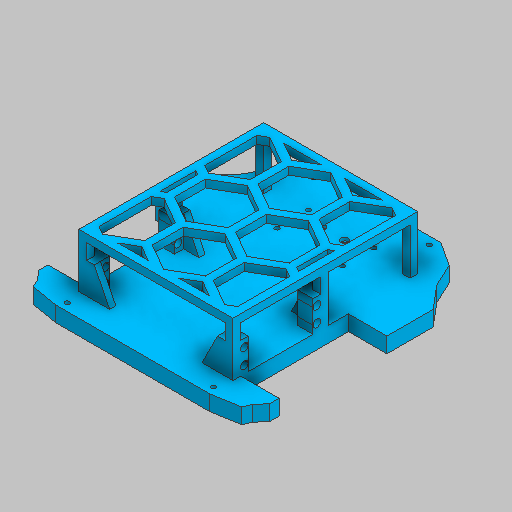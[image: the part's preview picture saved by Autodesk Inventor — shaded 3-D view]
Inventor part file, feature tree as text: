
AUTODESK INVENTOR PART (.ipt)
format: ipt  version: 2025 (Build 290162010, 162A)  size: 1,139,712 bytes
history: native  units: mm
features: other x22, extrude x15, sketch x15
ambient origin geometry x8: Origin, YZ Plane, XZ Plane, XY Plane, X Axis, Y Axis, Z Axis, Center Point
bodies: Body1 (feature_tree)
feature tree (52):
  other  "Sólido1"
  extrude  "Base"  Depth=10.0mm TaperAngle=0.0deg
  extrude  "Llantas"  Depth=70.0mm
  extrude  "Carroceria"  Depth=75.0mm
  extrude  "Tornillos Chasis 1"  Depth=150.0mm
  extrude  "Tornillos Chasis 2"  Depth=10.0mm TaperAngle=0.0deg
  extrude  "Soporte Rueda 1"  Depth=30.0mm
  extrude  "Soporte Rueda 2"  Depth=40.0mm
  extrude  "Soporte Motor 1"  Depth=15.0mm
  extrude  "Soporte Motor 2"  Depth=6.0mm
  extrude  "Soporte Motor 3"  Depth=11.34464mm
  extrude  "Soporte Motor 4"  Depth=5.0mm
  extrude  "Soporte ESP 1"  Depth=5.0mm
  extrude  "Soporte ESP 2"  Depth=37.5mm
  extrude  "Extrusión38"  Depth=5.0mm
  extrude  "Extrusión39"  Depth=10.0mm TaperAngle=0.0deg
  sketch  "Boceto Base"  dims[d44=37.5mm d45=3.0mm]
  sketch  "Boceto Llantas"  dims[d46=5.0mm d47=3.0mm]
  sketch  "Boceto Carroceria"  dims[d48=47.5mm d49=10.0mm d50=0.0mm d81=5.0mm d82=5.0mm d83=5.0mm d84=5.0mm d85=2.0mm d86=0.0mm d244=10.0mm d245=10.0mm d247=10.0mm d248=10.0mm d249=5.0mm d250=42.0mm d251=20.0mm d252=0.0mm d253=5.0mm d254=5.0mm d255=5.0mm d256=5.0mm d257=5.0mm d258=5.0mm d259=10.0mm d260=10.0mm d261=100.0mm d262=0.0mm d263=4.0mm d264=4.0mm d265=10.0mm d266=10.0mm d267=20.0mm d268=0.0mm d269=10.0mm d270=10.0mm d271=100.0mm d272=0.0mm d273=3.0mm d274=35.0mm d275=21.3mm d276=21.3mm d277=3.0mm d278=20.3mm d279=20.0mm d280=0.0mm d281=5.0mm d282=5.0mm d283=5.0mm d284=5.0mm d285=2.0mm d286=0.0mm d287=3.0mm d288=3.0mm d289=50.0mm d290=50.0mm d291=7.5mm d292=7.5mm d293=20.0mm d294=0.0mm d299=5.0mm d300=5.0mm d301=2.0mm d302=0.0mm d303=115.0mm d304=0.0mm d305=5.0mm d306=5.0mm d307=30.0mm d308=0.0mm d329=20.0mm d330=20.0mm d331=120.0deg d332=20.0mm d333=120.0deg d334=20.0mm d335=120.0deg d336=20.0mm d337=120.0deg d338=20.0mm d339=120.0deg d340=0.0mm d341=0.0mm d354=5.0mm d355=0.0mm d64=0.5mm d65=0.872665mm d66=0.5mm d67=0.872665mm d229=0.5mm d230=0.872665mm d231=0.5mm d232=0.872665mm]
  sketch  "Boceto Tornillos Chasis 1"  dims[d0=160.0mm d2=10.0mm d3=0.0mm]
  sketch  "Boceto Tornillos Chasis 2"  dims[d4=70.0mm d5=70.0mm]
  sketch  "Boceto27"  dims[d6=20.0mm d7=75.0mm]
  sketch  "Boceto28"  dims[d8=80.0mm d9=150.0mm]
  sketch  "Boceto29"  dims[d10=25.0mm d11=10.0mm d12=0.0mm]
  sketch  "Boceto30"  dims[d13=30.0mm d14=8.726646mm]
  sketch  "Boceto31"  dims[d15=11.34464mm d16=40.0mm]
  sketch  "Boceto32"  dims[d17=15.0mm d18=15.0mm]
  sketch  "Boceto33"  dims[d19=6.0mm d20=50.0mm]
  sketch  "Boceto35"  dims[d21=8.726646mm d22=11.34464mm]
  sketch  "Boceto36"  dims[d23=6.0mm d24=5.0mm]
  sketch  "Boceto37"  dims[d25=10.0mm d26=0.0mm d43=5.0mm]
  other  "Finish1"
  other  "Finish2"
  other  "Finish3"
  other  "Finish4"
  other  "Finish5"
  other  "Finish6"
  other  "Finish7"
  other  "Finish8"
  other  "Finish9"
  other  "Finish10"
  other  "Finish11"
  other  "Finish12"
  other  "Finish13"
  other  "Finish14"
  other  "Finish15"
  other  "Finish16"
  other  "Finish17"
  other  "Finish18"
  other  "Finish19"
  other  "Finish20"
  other  "Finish21"
